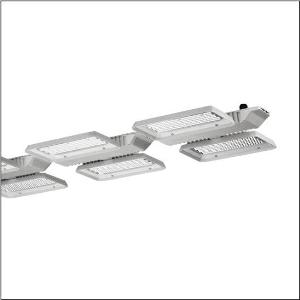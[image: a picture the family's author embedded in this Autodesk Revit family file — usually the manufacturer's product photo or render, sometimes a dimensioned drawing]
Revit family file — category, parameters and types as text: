
# Revit family: highbay_11_51hla1d34sca
name_source: partatom
category: Lighting Fixtures
units: mm (PartAtom-declared; Revit-internal decimal feet)

## family parameters
Cut with Voids When Loaded = No
Host = Face
Light Source = No
Part Type = Normal
Room Calculation Point = No
Round Connector Dimension = Use Diameter
Shared = No

## types (1)
- --- (1 x LED, 48560 lm, 284.4 W, 4000K)
    Apparent Load = 284 VA
    CIE Flux Codes = 88 95 99 100 99
    Color Rendering = 80
    Color Temperature = 4000K
    Default Elevation = 1800 mm
    Description = Highbay 11, LED high bay luminaire, primary light control with lens, of PMMA, light emission: direct distribution, primary light characteristic: symmetric, installation type: suspended mounting, for 3x 2x LED, rated luminous flux: 48.560lm, luminous efficacy: 171lm/W, light colour: 840, colour temperature: 4000K, control gear: ECG DALI, with terminal, 5-pole, max. 2.5mm², mains connection: 230..240V, AC, 50/60Hz, rated input power: 284W, LED unit, of diecast aluminium, unplated, bead blasted, silver, length: 1.410mm, width: 500mm, height: 65mm, housing, of diecast aluminium, uncoated, bead blasted, silver, protection rating (complete): IP65, insulation class (complete): insulation class I (protective earthing), certification: CE, ENEC, VDE, UKCA, protection symbol: D, impact resistance: IK08 with glass or PC cover, permissible operating ambient temperature: -35..+45°C, reducing of maximum allowable ambient temperature of 5°C with ceiling mounting, corresponds to IFS (International Featured Standards) requirements for safety and quality in the food industry, packaging unit: 1 piece
    Height = 95 mm
    Lamp = 1 x LED
    Lamp Light Flux = 48560 lm
    Lamp Power = 284.4 W
    Lamp count = 1
    Length = 1410 mm
    Luminous efficacy = 171 lm/W
    Manufacturer = Siteco
    ModVariant = No
    Model = 51HLA1D34SCA
    Mounting Place = Ceiling
    Mounting Type = Pendant
    Number of Poles = 1
    OnlyDefault = Yes
    Power Factor = 1
    Product Name = Highbay 11
    Product group = LED high bay luminaire
    ProductGroupID = 903
    Protection Class = Protection class I
    Protection Degree = IP 65
    RLX_Detail_Level = 1
    RLX_Emergency_Light_Flux = 0 lm
    RLX_Emergency_Type = 0
    RLX_Emergency_Type_DB = No
    RlxData = <blob elided: 105565 chars, md5=e6893d13>
    Socket = socket
    Standby Power = 0 W
    System Light Flux = 48560 lm
    System Power = 284 W
    Type Comments = factory setting: luminous flux: 100 % | dim-lin: 254 | 535 mA
    Type Image = l_1003314.jpg
    URL = http://relux.com
    VarID = @adj_146117
    Voltage = 0 V
    Weight = 0.00 kg
    Width = 501 mm

## geometry (parser evidence)
native form markers: Blend x4, Sweep x11
no freeform markers — native parametric forms only
